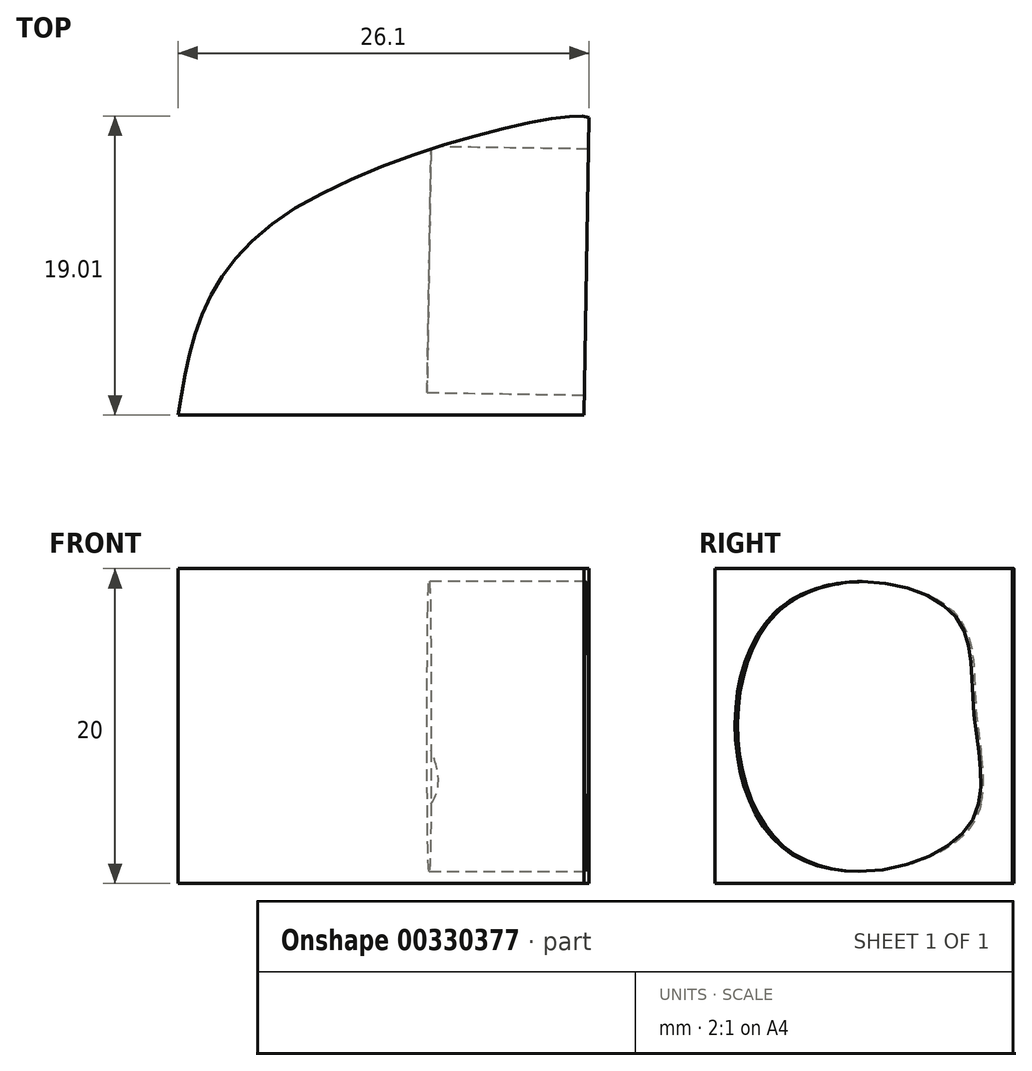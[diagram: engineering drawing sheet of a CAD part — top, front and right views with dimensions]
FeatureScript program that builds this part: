
annotation { "Feature Type Name" : "Feature", "Feature Type Description" : "" }
export const myFeature = defineFeature(function(context is Context, id is Id, definition is map)
    precondition{}
    {
        {
            var Q0;
            Q0=qCreatedBy(makeId("Top.planeOp"),FACE);
            var sketch = newSketch(context, id + "F0", { "sketchPlane" : qUnion([Q0])});
            skFitSpline(sketch, "E0", {"points": [v(-31.8, 9.15) * mm, v(-25.2, 21.75) * mm, v(-5.7, 28.05) * mm, v(-6, 27.45) * mm], "startDerivative": vector(5.33, 32.92) * mm, "endDerivative": vector(-7.58, -7.94) * mm});
            skLineSegment(sketch, "E1", {"start": v(-5.7, 28.05) * mm, "end": v(-6, 9.15) * mm});
            skLineSegment(sketch, "E2", {"start": v(-6, 9.15) * mm, "end": v(-31.8, 9.15) * mm});
            skSolve(sketch);
        }
        {
            var Q0;
            {var subQ0=sQuery(id+"F0.wireOp",EDGE,"E2");Q0=makeQuery(id+"F0.imprint","IMPRINT",FACE,{"disambiguationData":[TD([[makeQuery(id+"F0.imprint","IMPRINT",EDGE,{"derivedFrom":subQ0}),-1.0]])]});}
            extrude(context, id + "F1", {"entities" : qUnion([Q0]), "depth" : 20 * mm});
        }
        {
            var Q0;
            Q0=makeQuery(id+"F1.opExtrude","SWEPT_FACE",FACE,{"disambiguationData":[OSD([sQuery(id+"F0.wireOp",EDGE,"E1")])]});
            var sketch = newSketch(context, id + "F2", { "sketchPlane" : qUnion([Q0])});
            skFitSpline(sketch, "E3", {"points": [v(12.8, 17.16) * mm, v(23.88, 17.43) * mm, v(25.5, 10.81) * mm, v(24.96, 3.38) * mm, v(13.34, 2.3) * mm, v(12.8, 17.16) * mm]});
            skSolve(sketch);
        }
        {
            var Q0;
            Q0=makeQuery(id+"F2.imprint","IMPRINT",FACE,{"disambiguationData":[TD([[makeQuery(id+"F2.imprint","IMPRINT",EDGE,{"derivedFrom":sQuery(id+"F2.wireOp",EDGE,"E3")}),-1.0]])]});
            extrude(context, id + "F3", {"entities" : qUnion([Q0]), "operationType" : NewBodyOperationType.REMOVE, "oppositeDirection" : true, "depth" : 10 * mm});
        }
    });
